# Revit family: ALT2
name_source: partatom
category: Lighting Fixtures
units: mm (PartAtom-declared; Revit-internal decimal feet)

## family parameters
Always vertical = Yes
Cut with Voids When Loaded = No
Light Source = Yes
OmniClass Number = 23.80.70.14.21
OmniClass Title = Street and Roadway Lighting
Part Type = Normal
Room Calculation Point = No
Round Connector Dimension = Use Diameter
Shared = No
Work Plane-Based = No

## types (1)
- ALT2
    Apparent Load = 20 VA
    Assembly Code = D5020200
    Center Width = 3 "
    Certifications = UL Listed
    Color Filter = 16777215
    Color Temperature = 0 K
    Default Elevation = 0 "
    Depth = 18.44 "
    Description = Altitude® is the ultimate in luminaire design innovation with a unique balance of form, engineering and superior optics. The low profile housing is proportional and scalable with three sizes to cover more pedestrian/site/roadway environments than ever before. The result is an architecturally relevant luminaire of unsurpassed quality and flexibility that maximizes the power and performance.
    Dimming Lamp Color Temperature Shift = <None>
    Emit Shape Visible in Rendering = No
    Emit from Rectangle Length = 20 "
    Emit from Rectangle Width = 15 "
    Finish = Powder Coat-Black
    Fixture Height = 7.5 "
    Lamp = default
    Lens = Glass-Temper Molded
    Manufacturer = KIM Lighting
    Model = ALT2
    Number of Poles = 1
    Offset From Pole = 6.12 "
    Photometric Notes = More IES files download on Photometric Web Link
    Photometric Web File = ALT2-100L-160-3K7-2-BC.ies
    Pole = Yes
    Pole Width = 4 "
    Power Factor = 1
    Series = Altitude
    Tilt Angle = 90.00°
    Type Comments = Lighting Fixture
    URL = https://www.currentlighting.com
    Voltage = 0 V
    Wattage Comments = 20W
    Width = 14 "

## geometry (parser evidence)
native form markers: Sweep x8
no freeform markers — native parametric forms only
